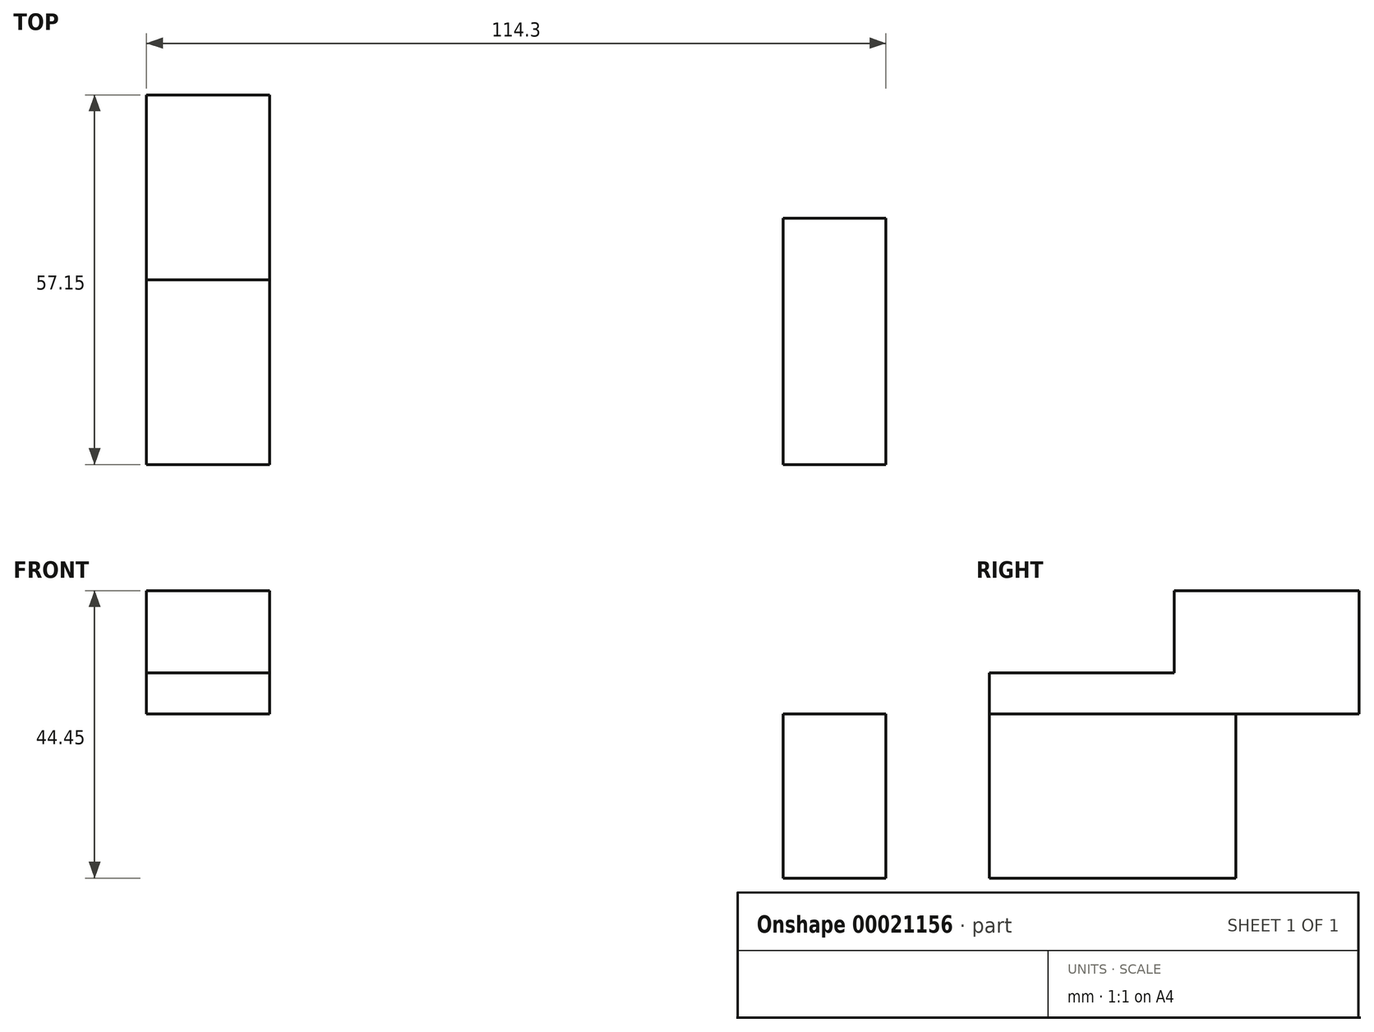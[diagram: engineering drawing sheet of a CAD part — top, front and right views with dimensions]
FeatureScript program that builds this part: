
annotation { "Feature Type Name" : "Feature", "Feature Type Description" : "" }
export const myFeature = defineFeature(function(context is Context, id is Id, definition is map)
    precondition{}
    {
        {
            var Q0;
            Q0=qCreatedBy(makeId("Top.planeOp"),FACE);
            var sketch = newSketch(context, id + "F0", { "sketchPlane" : qUnion([Q0])});
            skLineSegment(sketch, "E0.bottom", {"start": v(-83.76, -41.96) * mm, "end": v(30.54, -41.96) * mm});
            skLineSegment(sketch, "E0.top", {"start": v(-83.76, 15.19) * mm, "end": v(30.54, 15.19) * mm});
            skLineSegment(sketch, "E0.left", {"start": v(-83.76, -41.96) * mm, "end": v(-83.76, 15.19) * mm});
            skLineSegment(sketch, "E0.right", {"start": v(30.54, -41.96) * mm, "end": v(30.54, 15.19) * mm});
            skLineSegment(sketch, "E1.bottom", {"start": v(30.54, -41.96) * mm, "end": v(14.66, -41.96) * mm});
            skLineSegment(sketch, "E1.top", {"start": v(30.54, -3.86) * mm, "end": v(14.66, -3.86) * mm});
            skLineSegment(sketch, "E1.left", {"start": v(30.54, -41.96) * mm, "end": v(30.54, -3.86) * mm});
            skLineSegment(sketch, "E1.right", {"start": v(14.66, -41.96) * mm, "end": v(14.66, -3.86) * mm});
            skCircle(sketch, "E2", {"center": v(-22.37, -18) * mm, "radius": 11.11 * mm});
            skLineSegment(sketch, "E3", {"start": v(-26.61, 15.19) * mm, "end": v(-50.42, 15.19) * mm});
            skSolve(sketch);
        }
        {
            var Q0;
            Q0=makeQuery(id+"F0.imprint","IMPRINT",FACE,{"disambiguationData":[TD([[makeQuery(id+"F0.imprint","IMPRINT",EDGE,{"derivedFrom":sQuery(id+"F0.wireOp",EDGE,"E0.bottom")}),1.0]])]});
            extrude(context, id + "F1", {"entities" : qUnion([Q0]), "depth" : 25.4 * mm});
        }
        {
            var Q0;
            Q0=makeQuery(id+"F1.opExtrude","CAP_FACE",FACE,{"disambiguationData":[OSD([sQuery(id+"F0.wireOp",EDGE,"E0.bottom"),sQuery(id+"F0.wireOp",EDGE,"E0.top"),sQuery(id+"F0.wireOp",EDGE,"E0.left"),sQuery(id+"F0.wireOp",EDGE,"E0.right"),sQuery(id+"F0.wireOp",EDGE,"E1.top"),sQuery(id+"F0.wireOp",EDGE,"E1.right"),sQuery(id+"F0.wireOp",EDGE,"E2")])],"isStart":false});
            var sketch = newSketch(context, id + "F2", { "sketchPlane" : qUnion([Q0])});
            skLineSegment(sketch, "E4.bottom", {"start": v(-83.76, -41.96) * mm, "end": v(-64.71, -41.96) * mm});
            skLineSegment(sketch, "E4.top", {"start": v(-83.76, -13.39) * mm, "end": v(-64.71, -13.39) * mm});
            skLineSegment(sketch, "E4.left", {"start": v(-83.76, -41.96) * mm, "end": v(-83.76, -13.39) * mm});
            skLineSegment(sketch, "E4.right", {"start": v(-64.71, -41.96) * mm, "end": v(-64.71, -13.39) * mm});
            skSolve(sketch);
        }
        {
            var Q0;
            Q0 = qSketchRegion(id + "F2", true);
            extrude(context, id + "F3", {"entities" : qUnion([Q0]), "operationType" : NewBodyOperationType.ADD, "depth" : 6.35 * mm});
        }
        {
            var Q0;
            Q0=makeQuery(id+"F1.opExtrude","CAP_FACE",FACE,{"disambiguationData":[OSD([sQuery(id+"F0.wireOp",EDGE,"E0.bottom"),sQuery(id+"F0.wireOp",EDGE,"E0.top"),sQuery(id+"F0.wireOp",EDGE,"E0.left"),sQuery(id+"F0.wireOp",EDGE,"E0.right"),sQuery(id+"F0.wireOp",EDGE,"E1.top"),sQuery(id+"F0.wireOp",EDGE,"E1.right"),sQuery(id+"F0.wireOp",EDGE,"E2")])],"isStart":false});
            var sketch = newSketch(context, id + "F4", { "sketchPlane" : qUnion([Q0])});
            skLineSegment(sketch, "E5.bottom", {"start": v(-83.76, 15.19) * mm, "end": v(-64.71, 15.19) * mm});
            skLineSegment(sketch, "E5.top", {"start": v(-83.76, -13.39) * mm, "end": v(-64.71, -13.39) * mm});
            skLineSegment(sketch, "E5.left", {"start": v(-83.76, 15.19) * mm, "end": v(-83.76, -13.39) * mm});
            skLineSegment(sketch, "E5.right", {"start": v(-64.71, 15.19) * mm, "end": v(-64.71, -13.39) * mm});
            skSolve(sketch);
        }
        {
            var Q0;
            Q0 = qSketchRegion(id + "F4", true);
            extrude(context, id + "F5", {"entities" : qUnion([Q0]), "operationType" : NewBodyOperationType.ADD, "depth" : 19.05 * mm});
        }
    });
